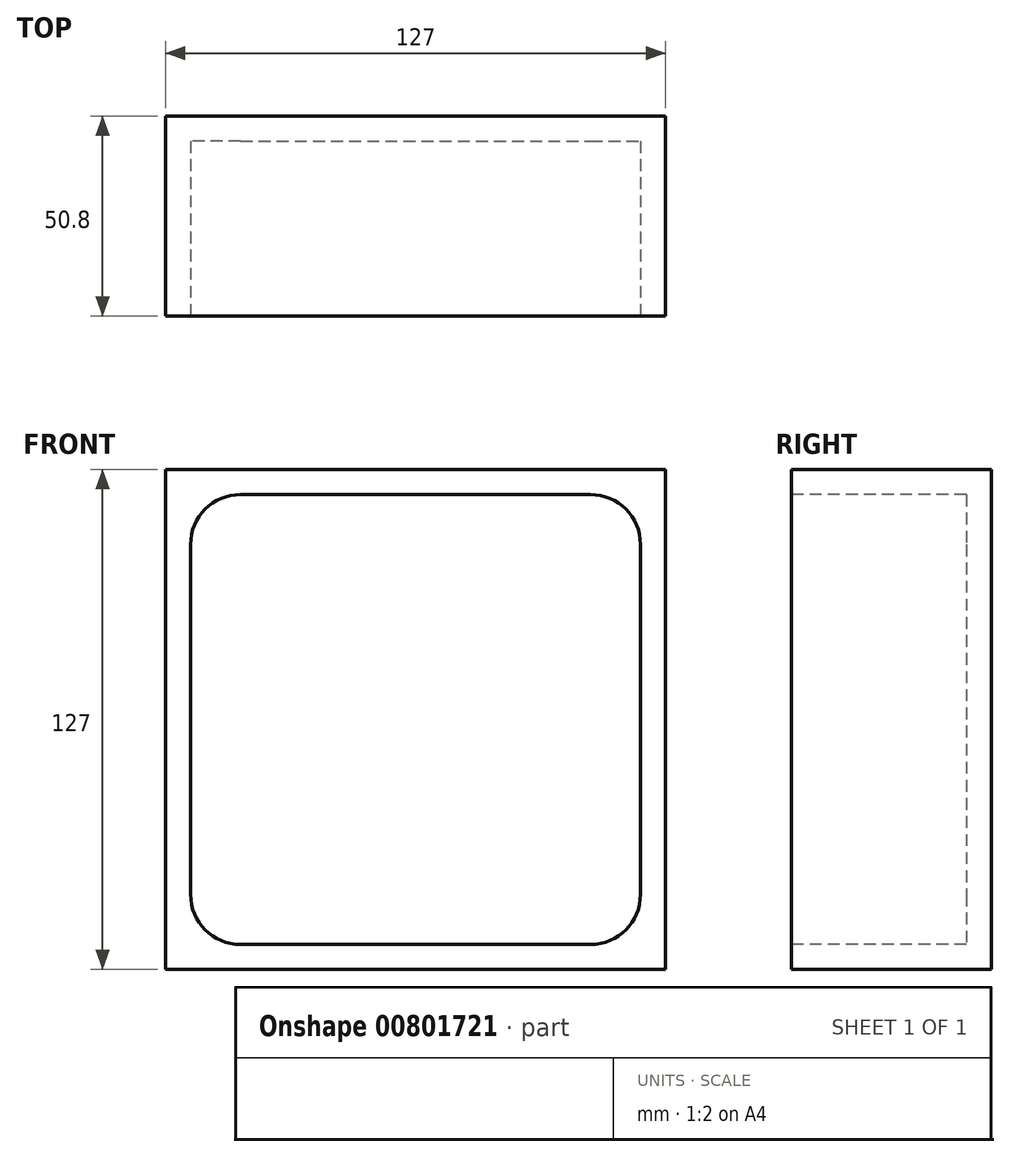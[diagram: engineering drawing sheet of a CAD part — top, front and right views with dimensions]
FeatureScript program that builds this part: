
annotation { "Feature Type Name" : "Feature", "Feature Type Description" : "" }
export const myFeature = defineFeature(function(context is Context, id is Id, definition is map)
    precondition{}
    {
        {
            var Q0;
            Q0=qCreatedBy(makeId("Front.planeOp"),FACE);
            var sketch = newSketch(context, id + "F0", { "sketchPlane" : qUnion([Q0])});
            skLineSegment(sketch, "E0.bottom", {"start": v(-67.76, 59.12) * mm, "end": v(59.24, 59.12) * mm});
            skLineSegment(sketch, "E0.top", {"start": v(-67.76, -67.88) * mm, "end": v(59.24, -67.88) * mm});
            skLineSegment(sketch, "E0.left", {"start": v(-67.76, 59.12) * mm, "end": v(-67.76, -67.88) * mm});
            skLineSegment(sketch, "E0.right", {"start": v(59.24, 59.12) * mm, "end": v(59.24, -67.88) * mm});
            skSolve(sketch);
        }
        {
            var Q0;
            Q0 = qSketchRegion(id + "F0", true);
            extrude(context, id + "F1", {"entities" : qUnion([Q0]), "depth" : 25.4 * mm, "offsetDistance" : 25.4 * mm, "hasSecondDirection" : true, "secondDirectionOppositeDirection" : true, "secondDirectionDepth" : 25.4 * mm});
        }
        {
            var Q0;
            Q0=makeQuery(id+"F1.opExtrude","CAP_FACE",FACE,{"disambiguationData":[OSD([sQuery(id+"F0.wireOp",EDGE,"E0.bottom"),sQuery(id+"F0.wireOp",EDGE,"E0.top"),sQuery(id+"F0.wireOp",EDGE,"E0.left"),sQuery(id+"F0.wireOp",EDGE,"E0.right")])],"isStart":false});
            var sketch = newSketch(context, id + "F2", { "sketchPlane" : qUnion([Q0])});
            skLineSegment(sketch, "E1.bottom", {"start": v(-61.41, 52.77) * mm, "end": v(52.89, 52.77) * mm});
            skLineSegment(sketch, "E1.top", {"start": v(-61.41, -61.53) * mm, "end": v(52.89, -61.53) * mm});
            skLineSegment(sketch, "E1.left", {"start": v(-61.41, 52.77) * mm, "end": v(-61.41, -61.53) * mm});
            skLineSegment(sketch, "E1.right", {"start": v(52.89, 52.77) * mm, "end": v(52.89, -61.53) * mm});
            skSolve(sketch);
        }
        {
            var Q0;
            Q0=makeQuery(id+"F2.imprint","IMPRINT",FACE,{"disambiguationData":[TD([[makeQuery(id+"F2.imprint","IMPRINT",EDGE,{"derivedFrom":sQuery(id+"F2.wireOp",EDGE,"E1.bottom")}),-1.0]])]});
            extrude(context, id + "F3", {"entities" : qUnion([Q0]), "operationType" : NewBodyOperationType.REMOVE, "oppositeDirection" : true, "depth" : 44.45 * mm, "offsetDistance" : 25.4 * mm});
        }
        {
            var Q0;
            Q0=makeQuery(id+"F3.boolean.opBoolean","COPY",EDGE,{"derivedFrom":makeQuery(id+"F3.opExtrude","SWEPT_EDGE",EDGE,{"disambiguationData":[OSD([sQuery(id+"F2.wireOp",EDGE,"E1.top"),sQuery(id+"F2.wireOp",EDGE,"E1.left")])]})});
            var Q1;
            Q1=makeQuery(id+"F3.boolean.opBoolean","COPY",EDGE,{"derivedFrom":makeQuery(id+"F3.opExtrude","SWEPT_EDGE",EDGE,{"disambiguationData":[OSD([sQuery(id+"F2.wireOp",EDGE,"E1.top"),sQuery(id+"F2.wireOp",EDGE,"E1.right")])]})});
            var Q2;
            Q2=makeQuery(id+"F3.boolean.opBoolean","COPY",EDGE,{"derivedFrom":makeQuery(id+"F3.opExtrude","SWEPT_EDGE",EDGE,{"disambiguationData":[OSD([sQuery(id+"F2.wireOp",EDGE,"E1.bottom"),sQuery(id+"F2.wireOp",EDGE,"E1.right")])]})});
            var Q3;
            Q3=makeQuery(id+"F3.boolean.opBoolean","COPY",EDGE,{"derivedFrom":makeQuery(id+"F3.opExtrude","SWEPT_EDGE",EDGE,{"disambiguationData":[OSD([sQuery(id+"F2.wireOp",EDGE,"E1.bottom"),sQuery(id+"F2.wireOp",EDGE,"E1.left")])]})});
            fillet(context, id + "F4", {"entities" : qUnion([Q0, Q1, Q2, Q3]), "radius" : 12.7 * mm, "tangentPropagation" : true, "allowEdgeOverflow" : false});
        }
    });
